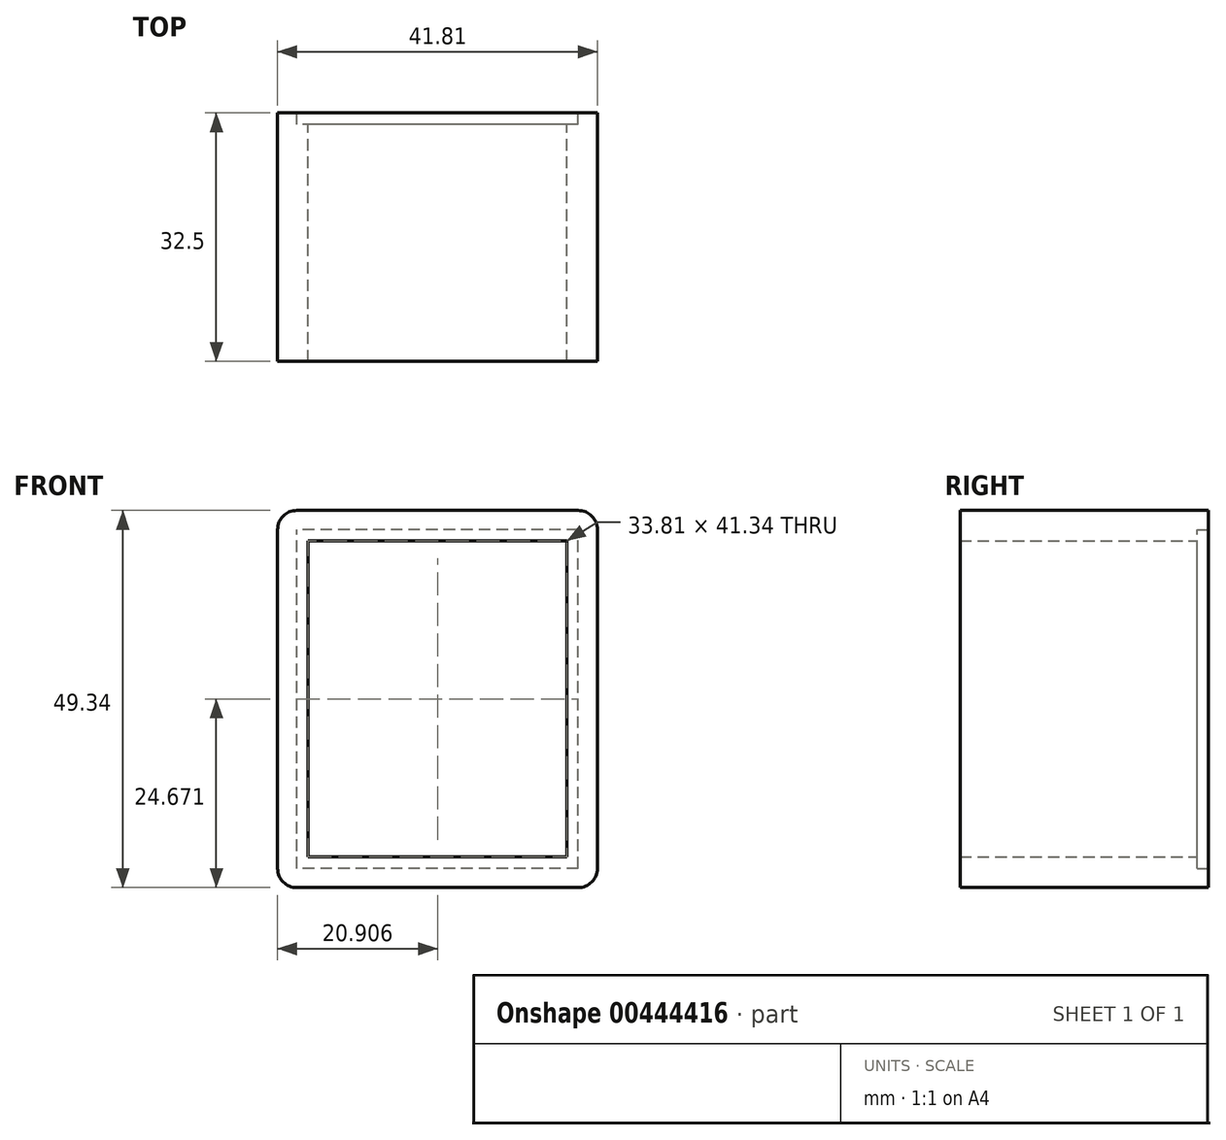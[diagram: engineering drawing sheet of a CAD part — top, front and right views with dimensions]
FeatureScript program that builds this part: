
annotation { "Feature Type Name" : "Feature", "Feature Type Description" : "" }
export const myFeature = defineFeature(function(context is Context, id is Id, definition is map)
    precondition{}
    {
        {
            var Q0;
            Q0=qCreatedBy(makeId("Front.planeOp"),FACE);
            var sketch = newSketch(context, id + "F0", { "sketchPlane" : qUnion([Q0])});
            skLineSegment(sketch, "E0.bottom", {"start": v(0, 0) * mm, "end": v(-41.8, 0) * mm});
            skLineSegment(sketch, "E0.top", {"start": v(0, 49.34) * mm, "end": v(-41.8, 49.34) * mm});
            skLineSegment(sketch, "E0.left", {"start": v(0, 0) * mm, "end": v(0, 49.34) * mm});
            skLineSegment(sketch, "E0.right", {"start": v(-41.8, 0) * mm, "end": v(-41.8, 49.34) * mm});
            skSolve(sketch);
        }
        {
            var Q0;
            Q0=makeQuery(id+"F0.imprint","IMPRINT",FACE,{"disambiguationData":[TD([[makeQuery(id+"F0.imprint","IMPRINT",EDGE,{"derivedFrom":sQuery(id+"F0.wireOp",EDGE,"E0.bottom")}),-1.0]])]});
            extrude(context, id + "F1", {"entities" : qUnion([Q0]), "depth" : 35 * mm});
        }
        {
            var Q0;
            Q0=makeQuery(id+"F1.opExtrude","CAP_FACE",FACE,{"disambiguationData":[OSD([sQuery(id+"F0.wireOp",EDGE,"E0.bottom"),sQuery(id+"F0.wireOp",EDGE,"E0.top"),sQuery(id+"F0.wireOp",EDGE,"E0.left"),sQuery(id+"F0.wireOp",EDGE,"E0.right")])],"isStart":false});
            shell(context, id + "F2", {"entities" : qUnion([Q0]), "thickness" : 4 * mm});
        }
        {
            var Q0;
            Q0=makeQuery(id+"F2.opShell","OFFSET_FACE",FACE,{"disambiguationData":[OSD([sQuery(id+"F0.wireOp",EDGE,"E0.bottom"),sQuery(id+"F0.wireOp",EDGE,"E0.top"),sQuery(id+"F0.wireOp",EDGE,"E0.left"),sQuery(id+"F0.wireOp",EDGE,"E0.right")])]});
            shell(context, id + "F3", {"entities" : qUnion([Q0]), "thickness" : 2.5 * mm});
        }
        {
            var Q0;
            Q0=makeQuery(id+"F1.opExtrude","CAP_FACE",FACE,{"disambiguationData":[OSD([sQuery(id+"F0.wireOp",EDGE,"E0.bottom"),sQuery(id+"F0.wireOp",EDGE,"E0.top"),sQuery(id+"F0.wireOp",EDGE,"E0.left"),sQuery(id+"F0.wireOp",EDGE,"E0.right")])],"isStart":true});
            extrude(context, id + "F4", {"entities" : qUnion([Q0]), "operationType" : NewBodyOperationType.REMOVE, "oppositeDirection" : true, "depth" : 2.5 * mm});
        }
        {
            var Q0;
            Q0=makeQuery(id+"F1.opExtrude","SWEPT_EDGE",EDGE,{"disambiguationData":[OSD([sQuery(id+"F0.wireOp",EDGE,"E0.top"),sQuery(id+"F0.wireOp",EDGE,"E0.right")])]});
            var Q1;
            Q1=makeQuery(id+"F1.opExtrude","SWEPT_EDGE",EDGE,{"disambiguationData":[OSD([sQuery(id+"F0.wireOp",EDGE,"E0.top"),sQuery(id+"F0.wireOp",EDGE,"E0.left")])]});
            var Q2;
            Q2=makeQuery(id+"F1.opExtrude","SWEPT_EDGE",EDGE,{"disambiguationData":[OSD([sQuery(id+"F0.wireOp",EDGE,"E0.bottom"),sQuery(id+"F0.wireOp",EDGE,"E0.left")])]});
            var Q3;
            Q3=makeQuery(id+"F1.opExtrude","SWEPT_EDGE",EDGE,{"disambiguationData":[OSD([sQuery(id+"F0.wireOp",EDGE,"E0.bottom"),sQuery(id+"F0.wireOp",EDGE,"E0.right")])]});
            fillet(context, id + "F5", {"entities" : qUnion([Q0, Q1, Q2, Q3]), "radius" : 2.5 * mm, "tangentPropagation" : true, "allowEdgeOverflow" : false});
        }
    });
